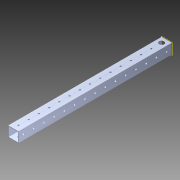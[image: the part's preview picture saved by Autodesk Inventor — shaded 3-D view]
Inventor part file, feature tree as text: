
AUTODESK INVENTOR PART (.ipt)
format: ipt  version: 2014 SP1 (Build 180222100, 222)  size: 1,239,552 bytes
history: native  units: in
note: dims shown in document units (in); Inventor stores cm internally (conversion verified against a paired STEP export)
features: extrude x2, sketch x2, pattern_circular x1, other x1, plane x1, imported_body x1
ambient origin geometry x8: Origin, YZ Plane, XZ Plane, XY Plane, X Axis, Y Axis, Z Axis, Center Point
bodies: Body1 (feature_tree)
feature tree (8):
  pattern_circular  "CirPattern2"
  other  "217-3426-STEP1"
  plane  "Work Plane1"
  extrude  "Extrusion1"  Depth=3937.0079in TaperAngle=0.0deg
  extrude  "Extrusion2"  Depth=0.5in
  imported_body  "Base1"
  sketch  "Sketch1"  dims[d0=-15.0in d1=3937.0079in d2=0.0in]
  sketch  "Sketch3"  dims[d4=3.937in d5=0.0in d6=0.5in d7=0.5in d8=0.5in]
